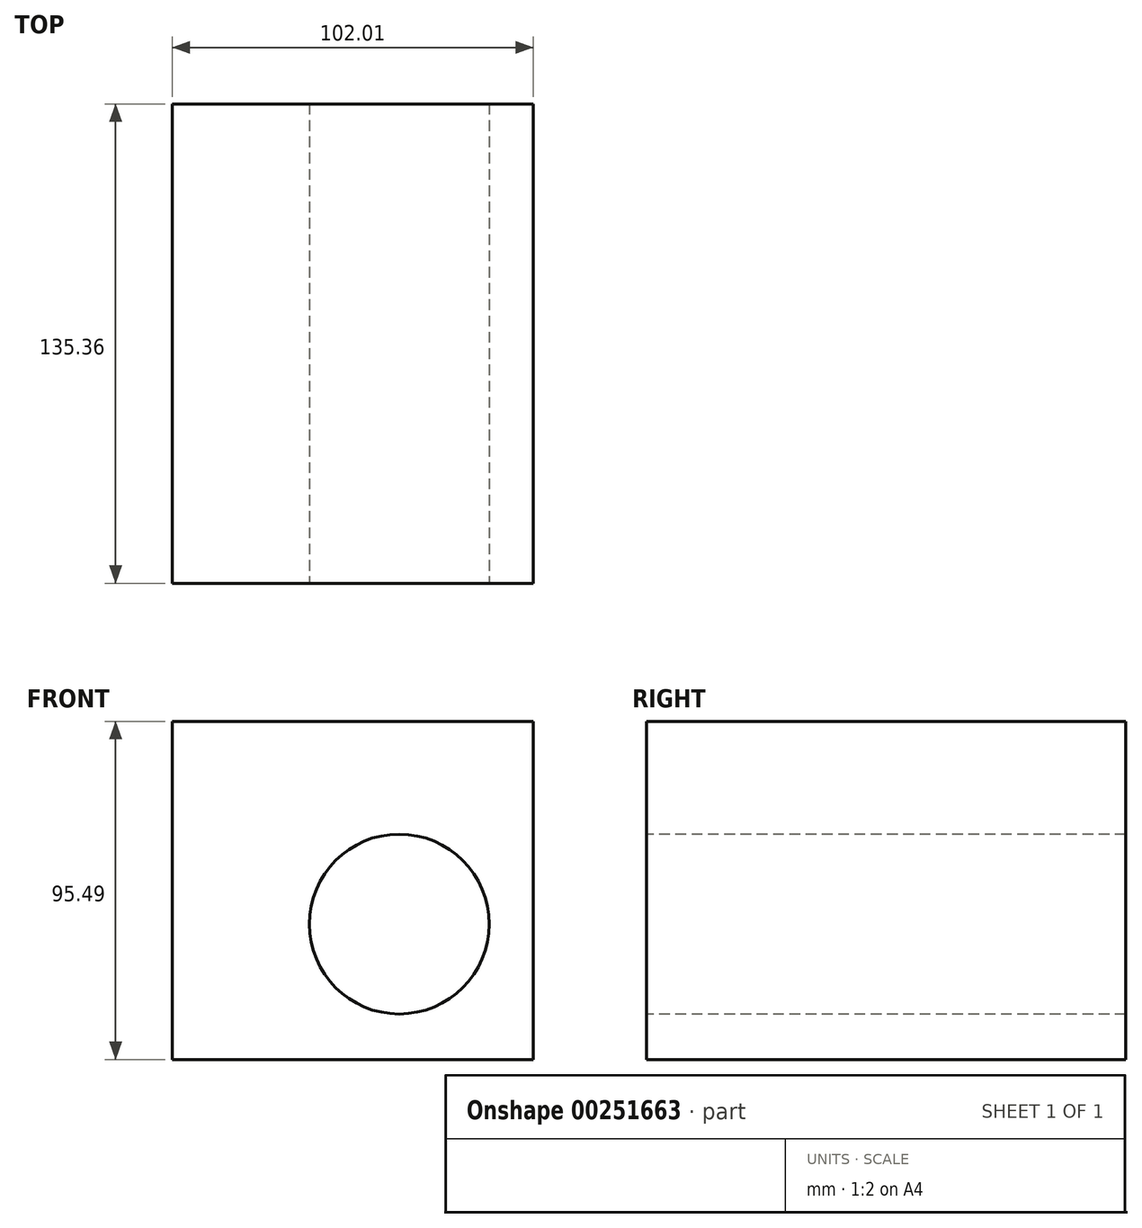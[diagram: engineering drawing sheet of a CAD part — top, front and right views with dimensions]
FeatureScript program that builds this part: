
annotation { "Feature Type Name" : "Feature", "Feature Type Description" : "" }
export const myFeature = defineFeature(function(context is Context, id is Id, definition is map)
    precondition{}
    {
        {
            var Q0;
            Q0=qCreatedBy(makeId("Front.planeOp"),FACE);
            var sketch = newSketch(context, id + "F0", { "sketchPlane" : qUnion([Q0])});
            skLineSegment(sketch, "E0.bottom", {"start": v(-64.13, 57.25) * mm, "end": v(37.88, 57.25) * mm});
            skLineSegment(sketch, "E0.top", {"start": v(-64.13, -38.24) * mm, "end": v(37.88, -38.24) * mm});
            skLineSegment(sketch, "E0.left", {"start": v(-64.13, 57.25) * mm, "end": v(-64.13, -38.24) * mm});
            skLineSegment(sketch, "E0.right", {"start": v(37.88, 57.25) * mm, "end": v(37.88, -38.24) * mm});
            skCircle(sketch, "E1", {"center": v(0, 0) * mm, "radius": 25.4 * mm});
            skSolve(sketch);
        }
        {
            var Q0;
            Q0=makeQuery(id+"F0.imprint","IMPRINT",FACE,{"disambiguationData":[TD([[makeQuery(id+"F0.imprint","IMPRINT",EDGE,{"derivedFrom":sQuery(id+"F0.wireOp",EDGE,"E0.bottom")}),-1.0]])]});
            extrude(context, id + "F1", {"entities" : qUnion([Q0]), "oppositeDirection" : true, "depth" : 135.36 * mm});
        }
    });
